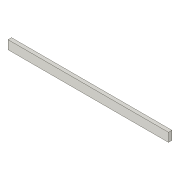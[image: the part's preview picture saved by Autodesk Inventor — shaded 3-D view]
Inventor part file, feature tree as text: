
AUTODESK INVENTOR PART (.ipt)
format: ipt  version: 2018 (Build 220112000, 112)  size: 74,240 bytes
history: native  units: in
note: dims shown in document units (in); Inventor stores cm internally (conversion verified against a paired STEP export)
features: extrude x1, plane x1, sketch x1
ambient origin geometry x8: Origin, YZ Plane, XZ Plane, XY Plane, X Axis, Y Axis, Z Axis, Center Point
bodies: Solid1 (feature_tree)
feature tree (3):
  extrude  "Extrusion1"  Depth=5.0in
  plane  "Work Plane1"
  sketch  "Sketch1"  dims[d0=2.0in d1=5.0in d2=92.0in d3=0.0in d4=-46.0in]
